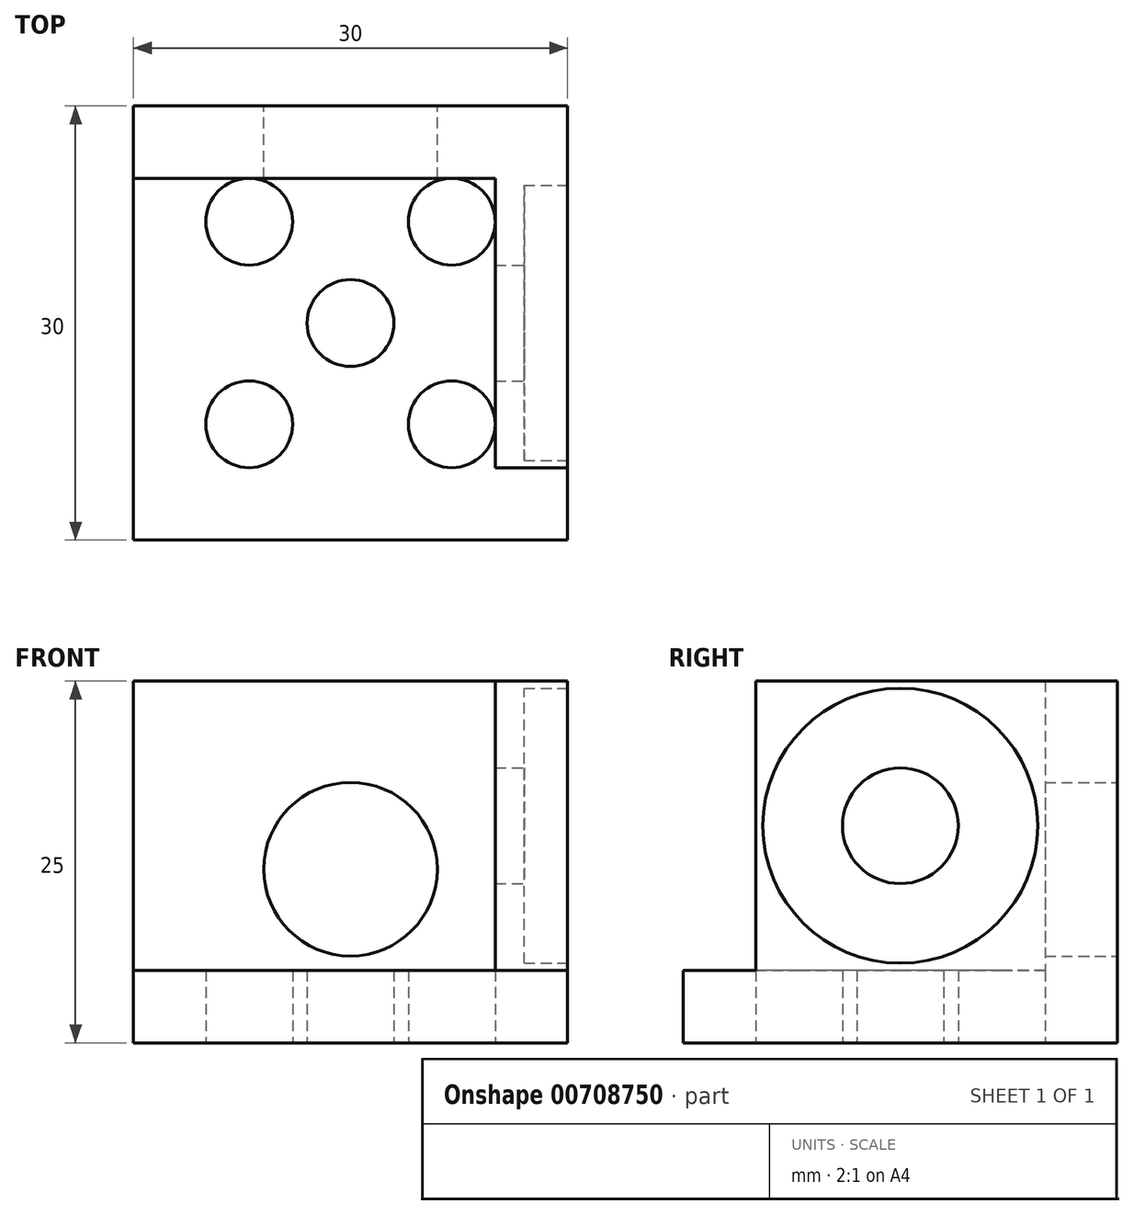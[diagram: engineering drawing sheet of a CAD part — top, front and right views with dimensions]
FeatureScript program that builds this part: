
annotation { "Feature Type Name" : "Feature", "Feature Type Description" : "" }
export const myFeature = defineFeature(function(context is Context, id is Id, definition is map)
    precondition{}
    {
        {
            var Q0;
            Q0=qCreatedBy(makeId("Top.planeOp"),FACE);
            var sketch = newSketch(context, id + "F0", { "sketchPlane" : qUnion([Q0])});
            skLineSegment(sketch, "E0.bottom", {"start": v(15, 15) * mm, "end": v(-15, 15) * mm});
            skLineSegment(sketch, "E0.top", {"start": v(15, -15) * mm, "end": v(-15, -15) * mm});
            skLineSegment(sketch, "E0.left", {"start": v(15, 15) * mm, "end": v(15, -15) * mm});
            skLineSegment(sketch, "E0.right", {"start": v(-15, 15) * mm, "end": v(-15, -15) * mm});
            skPoint(sketch, "E0.middle", {"position": v(0, 0) * mm});
            skLineSegment(sketch, "E1", {"start": v(22.37, 0) * mm, "end": v(-26.37, 0) * mm, "construction": true});
            skPoint(sketch, "E1.startSnap0", {"position": v(15, 0) * mm});
            skPoint(sketch, "E1.endSnap0", {"position": v(15, 0) * mm});
            skLineSegment(sketch, "E2", {"start": v(0, 19.5) * mm, "end": v(0, -22.26) * mm, "construction": true});
            skCircle(sketch, "E3", {"center": v(0, 0) * mm, "radius": 3 * mm});
            skCircle(sketch, "E4", {"center": v(7, 7) * mm, "radius": 3 * mm});
            skCircle(sketch, "E5", {"center": v(-7, 7) * mm, "radius": 3 * mm});
            skCircle(sketch, "E6", {"center": v(-7, -7) * mm, "radius": 3 * mm});
            skCircle(sketch, "E7", {"center": v(7, -7) * mm, "radius": 3 * mm});
            skSolve(sketch);
        }
        {
            var Q0;
            Q0=makeQuery(id+"F0.imprint","IMPRINT",FACE,{"disambiguationData":[TD([[makeQuery(id+"F0.imprint","IMPRINT",EDGE,{"derivedFrom":sQuery(id+"F0.wireOp",EDGE,"E0.bottom")}),1.0]])]});
            extrude(context, id + "F1", {"entities" : qUnion([Q0]), "depth" : 5 * mm, "offsetDistance" : 25 * mm});
        }
        {
            var Q0;
            Q0=makeQuery(id+"F1.opExtrude","SWEPT_FACE",FACE,{"disambiguationData":[OSD([sQuery(id+"F0.wireOp",EDGE,"E0.left")])]});
            var sketch = newSketch(context, id + "F2", { "sketchPlane" : qUnion([Q0])});
            skLineSegment(sketch, "E8.bottom", {"start": v(15, 5) * mm, "end": v(-10, 5) * mm});
            skLineSegment(sketch, "E8.top", {"start": v(15, 25) * mm, "end": v(-10, 25) * mm});
            skLineSegment(sketch, "E8.left", {"start": v(15, 5) * mm, "end": v(15, 25) * mm});
            skLineSegment(sketch, "E8.right", {"start": v(-10, 5) * mm, "end": v(-10, 25) * mm});
            skCircle(sketch, "E9", {"center": v(0, 15) * mm, "radius": 9.5 * mm});
            skSolve(sketch);
        }
        {
            var Q0;
            Q0=makeQuery(id+"F2.imprint","IMPRINT",FACE,{"disambiguationData":[TD([[makeQuery(id+"F2.imprint","IMPRINT",EDGE,{"derivedFrom":sQuery(id+"F2.wireOp",EDGE,"E8.bottom")}),-1.0]])]});
            extrude(context, id + "F3", {"entities" : qUnion([Q0]), "operationType" : NewBodyOperationType.ADD, "oppositeDirection" : true, "depth" : 3 * mm, "offsetDistance" : 25 * mm});
        }
        {
            var Q0;
            Q0=makeQuery(id+"F3.opExtrude","CAP_FACE",FACE,{"disambiguationData":[OSD([sQuery(id+"F2.wireOp",EDGE,"E8.bottom"),sQuery(id+"F2.wireOp",EDGE,"E8.top"),sQuery(id+"F2.wireOp",EDGE,"E8.left"),sQuery(id+"F2.wireOp",EDGE,"E8.right"),sQuery(id+"F2.wireOp",EDGE,"E9")])],"isStart":false});
            var sketch = newSketch(context, id + "F4", { "sketchPlane" : qUnion([Q0])});
            skLineSegment(sketch, "E10.bottom", {"start": v(10, 25) * mm, "end": v(-15, 25) * mm});
            skLineSegment(sketch, "E10.top", {"start": v(10, 5) * mm, "end": v(-15, 5) * mm});
            skLineSegment(sketch, "E10.left", {"start": v(10, 25) * mm, "end": v(10, 5) * mm});
            skLineSegment(sketch, "E10.right", {"start": v(-15, 25) * mm, "end": v(-15, 5) * mm});
            skCircle(sketch, "E11", {"center": v(0, 15) * mm, "radius": 4 * mm});
            skSolve(sketch);
        }
        {
            var Q0;
            Q0 = qSketchRegion(id + "F4", true);
            extrude(context, id + "F5", {"entities" : qUnion([Q0]), "operationType" : NewBodyOperationType.ADD, "depth" : 2 * mm, "offsetDistance" : 25 * mm});
        }
        {
            var Q0;
            Q0=makeQuery(id+"F5.boolean.opBoolean","MERGE",FACE,{"derivedFrom":[makeQuery(id+"F3.boolean.opBoolean","MERGE",FACE,{"derivedFrom":[makeQuery(id+"F1.opExtrude","SWEPT_FACE",FACE,{"disambiguationData":[OSD([sQuery(id+"F0.wireOp",EDGE,"E0.bottom")])]}),makeQuery(id+"F3.opExtrude","SWEPT_FACE",FACE,{"disambiguationData":[OSD([sQuery(id+"F2.wireOp",EDGE,"E8.left")])]})]}),makeQuery(id+"F5.opExtrude","SWEPT_FACE",FACE,{"disambiguationData":[OSD([sQuery(id+"F4.wireOp",EDGE,"E10.right")])]})]});
            var sketch = newSketch(context, id + "F6", { "sketchPlane" : qUnion([Q0])});
            skLineSegment(sketch, "E12.bottom", {"start": v(-15, 25) * mm, "end": v(15, 25) * mm});
            skLineSegment(sketch, "E12.top", {"start": v(-15, 5) * mm, "end": v(15, 5) * mm});
            skLineSegment(sketch, "E12.left", {"start": v(-15, 25) * mm, "end": v(-15, 5) * mm});
            skLineSegment(sketch, "E12.right", {"start": v(15, 25) * mm, "end": v(15, 5) * mm});
            skCircle(sketch, "E13", {"center": v(0, 12) * mm, "radius": 6 * mm});
            skSolve(sketch);
        }
        {
            var Q0;
            {var subQ2=sQuery(id+"F6.wireOp",EDGE,"E12.right");Q0=makeQuery(id+"F6.imprint","IMPRINT",FACE,{"disambiguationData":[TD([[makeQuery(id+"F6.imprint","IMPRINT",EDGE,{"derivedFrom":subQ2}),-1.0]])]});}
            extrude(context, id + "F7", {"entities" : qUnion([Q0]), "operationType" : NewBodyOperationType.ADD, "oppositeDirection" : true, "depth" : 5 * mm, "offsetDistance" : 25 * mm});
        }
        {
            var Q0;
            Q0=makeQuery(id+"F1.opExtrude","CAP_FACE",FACE,{"disambiguationData":[OSD([sQuery(id+"F0.wireOp",EDGE,"E0.bottom"),sQuery(id+"F0.wireOp",EDGE,"E0.top"),sQuery(id+"F0.wireOp",EDGE,"E0.left"),sQuery(id+"F0.wireOp",EDGE,"E0.right"),sQuery(id+"F0.wireOp",EDGE,"E3"),sQuery(id+"F0.wireOp",EDGE,"E4"),sQuery(id+"F0.wireOp",EDGE,"E5"),sQuery(id+"F0.wireOp",EDGE,"E6"),sQuery(id+"F0.wireOp",EDGE,"E7")])],"isStart":true});
            cPlane(context, id + "F8", {"entities" : qUnion([Q0]), "cplaneType" : CPlaneType.OFFSET, "offset" : 12 * mm, "oppositeDirection" : true, "width" : 150 * mm, "height" : 150 * mm});
        }
    });
